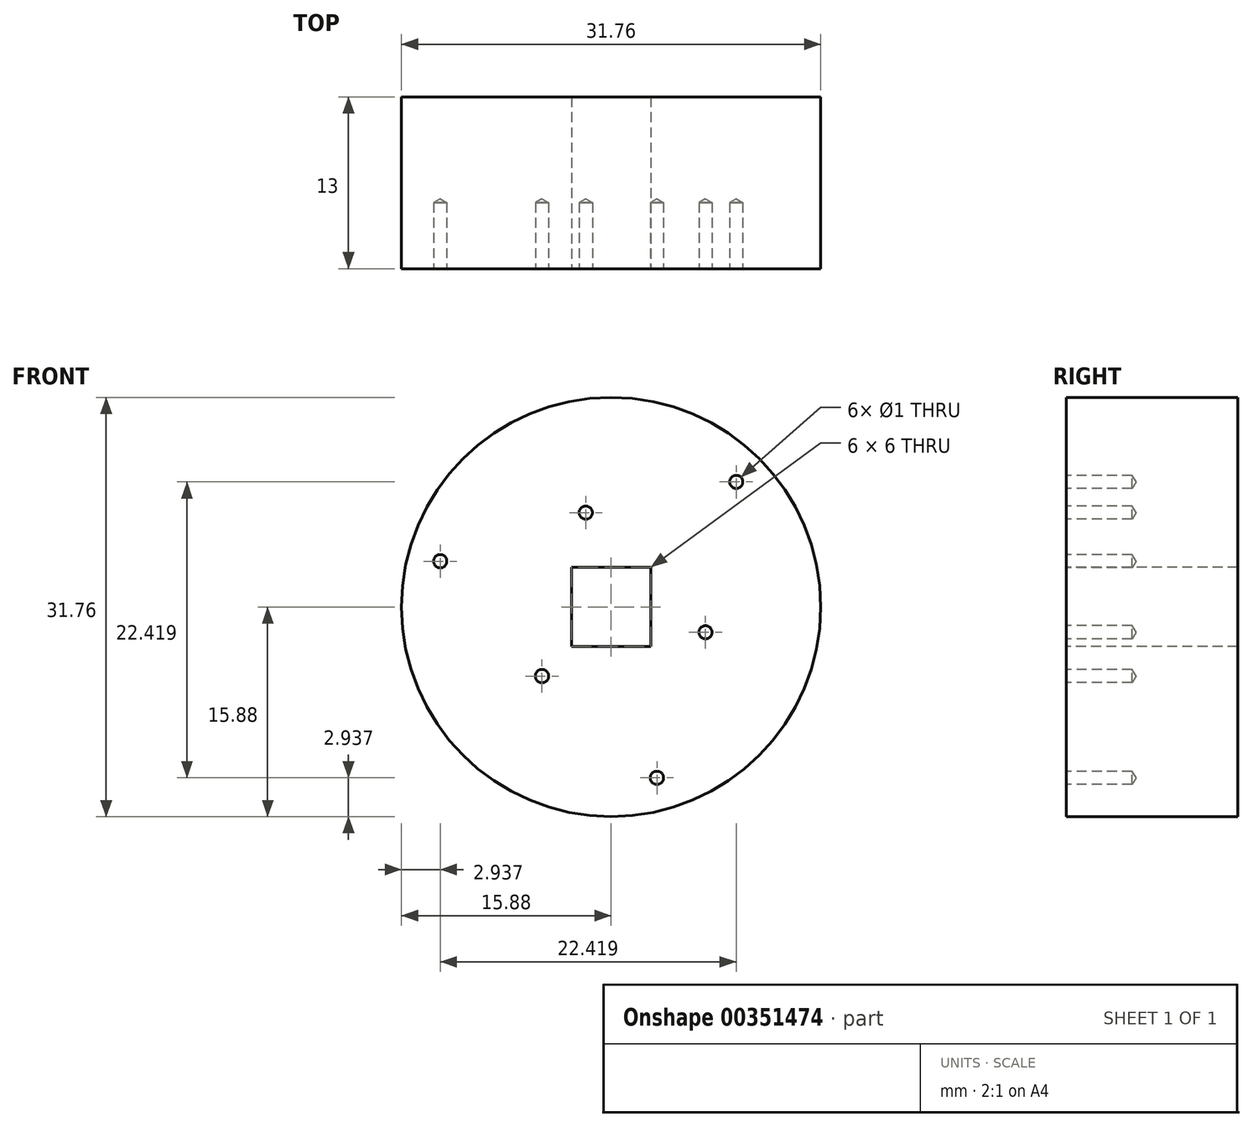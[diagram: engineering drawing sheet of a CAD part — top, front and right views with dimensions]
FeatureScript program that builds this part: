
annotation { "Feature Type Name" : "Feature", "Feature Type Description" : "" }
export const myFeature = defineFeature(function(context is Context, id is Id, definition is map)
    precondition{}
    {
        {
            var Q0;
            Q0=qCreatedBy(makeId("Front.planeOp"),FACE);
            var sketch = newSketch(context, id + "F0", { "sketchPlane" : qUnion([Q0])});
            skCircle(sketch, "E0", {"center": v(0, 0) * mm, "radius": 15.88 * mm});
            skSolve(sketch);
        }
        {
            var Q0;
            Q0 = qSketchRegion(id + "F0", true);
            extrude(context, id + "F1", {"entities" : qUnion([Q0]), "oppositeDirection" : true, "depth" : 13 * mm});
        }
        {
            var Q0;
            Q0=qCreatedBy(makeId("Front.planeOp"),FACE);
            var sketch = newSketch(context, id + "F2", { "sketchPlane" : qUnion([Q0])});
            skLineSegment(sketch, "E1.bottom", {"start": v(-3, 3) * mm, "end": v(3, 3) * mm});
            skLineSegment(sketch, "E1.top", {"start": v(-3, -3) * mm, "end": v(3, -3) * mm});
            skLineSegment(sketch, "E1.left", {"start": v(-3, 3) * mm, "end": v(-3, -3) * mm});
            skLineSegment(sketch, "E1.right", {"start": v(3, 3) * mm, "end": v(3, -3) * mm});
            skSolve(sketch);
        }
        {
            var Q0;
            Q0 = qSketchRegion(id + "F2", true);
            extrude(context, id + "F3", {"entities" : qUnion([Q0]), "operationType" : NewBodyOperationType.REMOVE, "endBound" : BoundingType.THROUGH_ALL, "oppositeDirection" : true, "depth" : 25 * mm});
        }
        {
            var Q0;
            Q0=qCreatedBy(makeId("Front.planeOp"),FACE);
            var sketch = newSketch(context, id + "F4", { "sketchPlane" : qUnion([Q0])});
            skPoint(sketch, "E2", {"position": v(9.48, 9.48) * mm});
            skLineSegment(sketch, "E3", {"start": v(0, 0) * mm, "end": v(9.48, 9.48) * mm, "construction": true});
            skPoint(sketch, "E4.1.0", {"position": v(3.47, -12.94) * mm});
            skPoint(sketch, "E4.2.0", {"position": v(-12.94, 3.47) * mm});
            skPoint(sketch, "E4.center", {"position": v(0, 0) * mm});
            skLineSegment(sketch, "E4.anchor2", {"start": v(0, 0) * mm, "end": v(-12.94, 3.47) * mm, "construction": true});
            skSolve(sketch);
        }
        {
            var Q0;
            Q0=qCreatedBy(makeId("Front.planeOp"),FACE);
            var sketch = newSketch(context, id + "F5", { "sketchPlane" : qUnion([Q0])});
            skPoint(sketch, "E5", {"position": v(7.15, -1.92) * mm});
            skLineSegment(sketch, "E6", {"start": v(0, 0) * mm, "end": v(7.15, -1.92) * mm, "construction": true});
            skPoint(sketch, "E7.1.0", {"position": v(-1.92, 7.15) * mm});
            skPoint(sketch, "E7.2.0", {"position": v(-5.23, -5.23) * mm});
            skPoint(sketch, "E7.center", {"position": v(0, 0) * mm});
            skSolve(sketch);
        }
        {
            var Q0;
            Q0=sQuery(id+"F4.wireOp",VERTEX,"E2");
            var Q1;
            Q1=sQuery(id+"F4.wireOp",VERTEX,"E4.1.0");
            var Q2;
            Q2=sQuery(id+"F4.wireOp",VERTEX,"E4.2.0");
            var Q3;
            Q3=sQuery(id+"F5.wireOp",VERTEX,"E7.1.0");
            var Q4;
            Q4=sQuery(id+"F5.wireOp",VERTEX,"E5");
            var Q5;
            Q5=sQuery(id+"F5.wireOp",VERTEX,"E7.2.0");
            var Q6;
            Q6=makeQuery(id+"F1.opExtrude","SWEPT_BODY",BODY,{"disambiguationData":[OSD([sQuery(id+"F0.wireOp",EDGE,"E0")])]});
            hole(context, id + "F6", {"style" : HoleStyle.SIMPLE, "endStyle" : HoleEndStyle.BLIND, "holeDiameter" : 1 * mm, "holeDepth" : 5 * mm, "isTappedThrough" : true, "tappedDepth" : 9.62 * mm, "tapClearance" : 3, "startFromSketch" : true, "locations" : qUnion([Q0, Q1, Q2, Q3, Q4, Q5]), "scope" : qUnion([Q6])});
        }
    });
